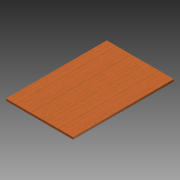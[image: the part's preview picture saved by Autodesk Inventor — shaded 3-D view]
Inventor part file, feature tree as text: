
AUTODESK INVENTOR PART (.ipt)
format: ipt  version: 2015 SP1 (Build 190203100, 203)  size: 98,304 bytes
history: native  units: mm
features: extrude x2, sketch x2, hole x1, pattern_linear x1
ambient origin geometry x8: Origin, YZ Plane, XZ Plane, XY Plane, X Axis, Y Axis, Z Axis, Center Point
bodies: Solid1 (feature_tree)
feature tree (6):
  extrude  "Extrusion1"  Depth=600.0mm
  hole  "Hole1"  [1 undecoded]
  pattern_linear  "Rectangular Pattern1"  Count1=2  [1 undecoded]
  extrude  "Extrusion2"  Depth=12.0mm
  sketch  "Sketch1"  dims[d0=400.0mm d1=600.0mm]
  sketch  "Sketch2"  dims[d2=12.0mm d3=0.0mm d4=15.0mm d5=15.0mm d6=8.0mm d7=6.0mm d8=12.0mm d9=4.0mm d10=90.0deg d11=8.0mm d12=20.594885mm d22=20.0mm d24=300.0mm d25=20.0mm d27=430.0mm d28=30.0mm d29=30.0mm d30=30.0mm d31=12.0mm d32=0.0mm d33=0.0mm]
note: 2 required parameter values undecoded (feature->parameter linkage not recoverable at this tier; creation-order binding heuristic only, values carry confidence <= 0.55)
